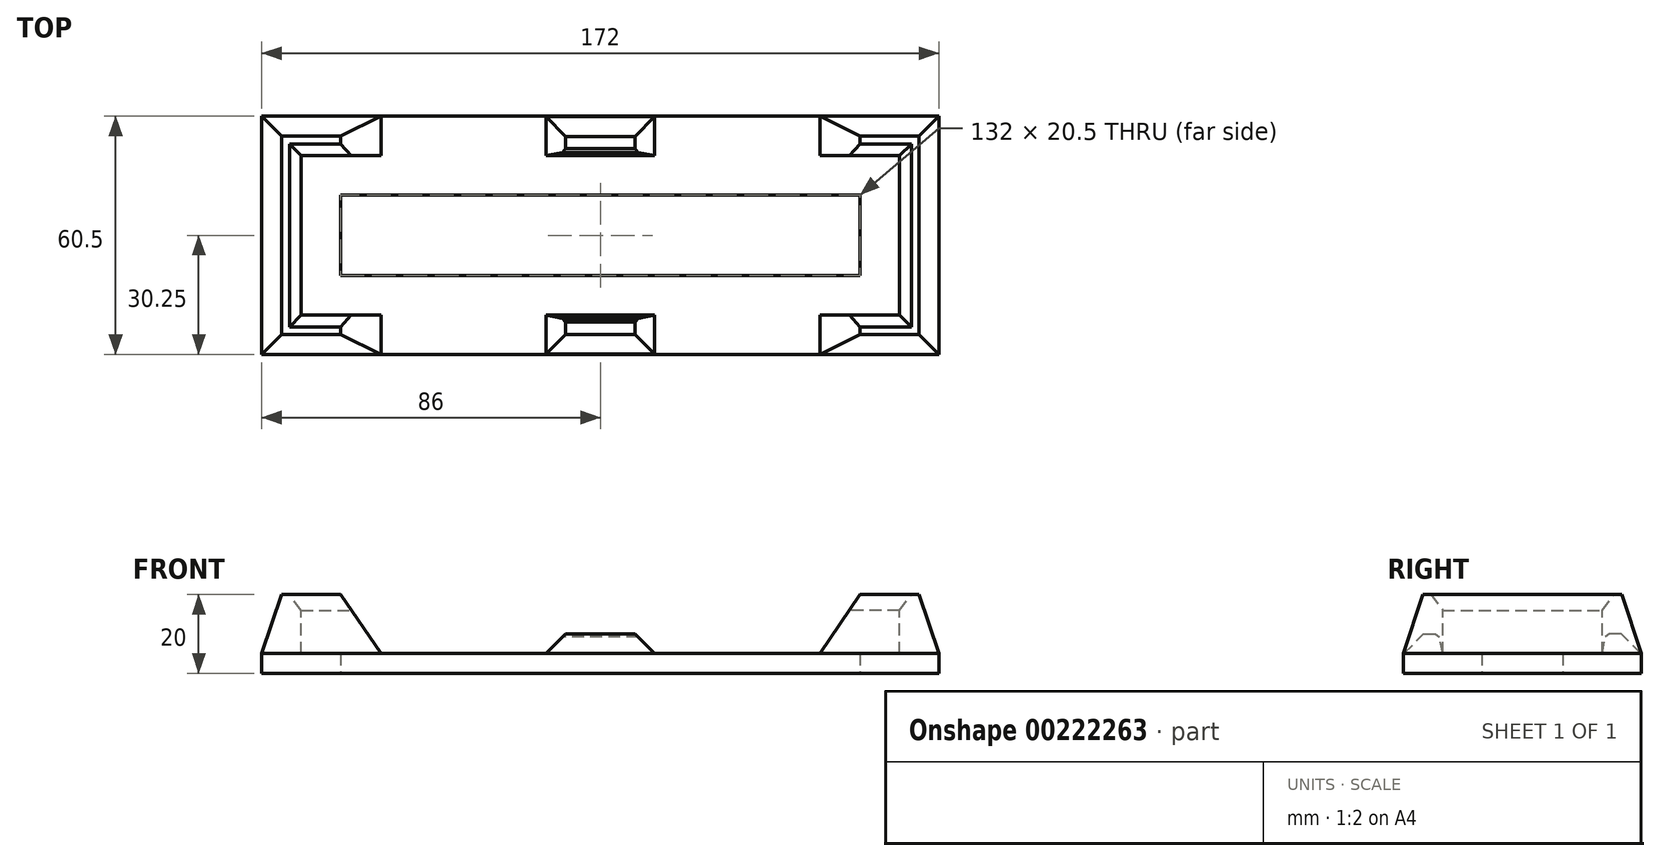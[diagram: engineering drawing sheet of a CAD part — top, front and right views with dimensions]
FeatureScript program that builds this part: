
annotation { "Feature Type Name" : "Feature", "Feature Type Description" : "" }
export const myFeature = defineFeature(function(context is Context, id is Id, definition is map)
    precondition{}
    {
        {
            var Q0;
            Q0=qCreatedBy(makeId("Top.planeOp"),FACE);
            var sketch = newSketch(context, id + "F0", { "sketchPlane" : qUnion([Q0])});
            skLineSegment(sketch, "E0.bottom", {"start": v(76, -20.25) * mm, "end": v(-76, -20.25) * mm, "construction": true});
            skLineSegment(sketch, "E0.top", {"start": v(76, 20.25) * mm, "end": v(-76, 20.25) * mm, "construction": true});
            skLineSegment(sketch, "E0.left", {"start": v(76, -20.25) * mm, "end": v(76, 20.25) * mm, "construction": true});
            skLineSegment(sketch, "E0.right", {"start": v(-76, -20.25) * mm, "end": v(-76, 20.25) * mm, "construction": true});
            skPoint(sketch, "E0.middle", {"position": v(0, 0) * mm});
            skLineSegment(sketch, "E1.bottom", {"start": v(86, -30.25) * mm, "end": v(-86, -30.25) * mm});
            skLineSegment(sketch, "E1.top", {"start": v(86, 30.25) * mm, "end": v(-86, 30.25) * mm});
            skLineSegment(sketch, "E1.left", {"start": v(86, -30.25) * mm, "end": v(86, 30.25) * mm});
            skLineSegment(sketch, "E1.right", {"start": v(-86, -30.25) * mm, "end": v(-86, 30.25) * mm});
            skSolve(sketch);
        }
        {
            var Q0;
            Q0=qCreatedBy(makeId("Top.planeOp"),FACE);
            cPlane(context, id + "F1", {"entities" : qUnion([Q0]), "cplaneType" : CPlaneType.OFFSET, "offset" : 15 * mm, "width" : 150 * mm, "height" : 150 * mm});
        }
        {
            var Q0;
            Q0=qCreatedBy(id+"F1.planeOp",FACE);
            var sketch = newSketch(context, id + "F2", { "sketchPlane" : qUnion([Q0])});
            skPoint(sketch, "E2.0", {"position": v(-86, -30.25) * mm});
            skPoint(sketch, "E3.0", {"position": v(-76, -20.25) * mm});
            skLineSegment(sketch, "E4", {"start": v(-76, 0) * mm, "end": v(-76, -20.25) * mm});
            skLineSegment(sketch, "E5", {"start": v(-76, -20.25) * mm, "end": v(-86, -30.25) * mm, "construction": true});
            skPoint(sketch, "E6", {"position": v(-81, -25.25) * mm});
            skLineSegment(sketch, "E7", {"start": v(-76, 0) * mm, "end": v(-81, 0) * mm});
            skLineSegment(sketch, "E8", {"start": v(-81, 0) * mm, "end": v(-81, -25.25) * mm});
            skLineSegment(sketch, "E9", {"start": v(-76, -20.25) * mm, "end": v(-66, -20.25) * mm});
            skLineSegment(sketch, "E10", {"start": v(-66, -20.25) * mm, "end": v(-66, -25.25) * mm});
            skLineSegment(sketch, "E11", {"start": v(-66, -25.25) * mm, "end": v(-81, -25.25) * mm});
            skSolve(sketch);
        }
        {
            var Q0;
            Q0=qCreatedBy(makeId("Top.planeOp"),FACE);
            var sketch = newSketch(context, id + "F3", { "sketchPlane" : qUnion([Q0])});
            skPoint(sketch, "E12.0", {"position": v(-86, -30.25) * mm});
            skPoint(sketch, "E13.0", {"position": v(-76, -20.25) * mm});
            skLineSegment(sketch, "E14", {"start": v(-86, -30.25) * mm, "end": v(-86, 0) * mm});
            skLineSegment(sketch, "E15", {"start": v(-86, 0) * mm, "end": v(-76, 0) * mm});
            skLineSegment(sketch, "E16", {"start": v(-76, 0) * mm, "end": v(-76, -20.25) * mm});
            skLineSegment(sketch, "E17", {"start": v(-76, -20.25) * mm, "end": v(-86, -30.25) * mm, "construction": true});
            skLineSegment(sketch, "E18.MirrorCS", {"start": v(-55.75, -20.25) * mm, "end": v(-76, -20.25) * mm});
            skLineSegment(sketch, "E19.MirrorCS", {"start": v(-86, -30.25) * mm, "end": v(-55.75, -30.25) * mm});
            skLineSegment(sketch, "E20.MirrorCS", {"start": v(-55.75, -30.25) * mm, "end": v(-55.75, -20.25) * mm});
            skLineSegment(sketch, "E21", {"start": v(0, 0) * mm, "end": v(-88.2, 0) * mm, "construction": true});
            skSolve(sketch);
        }
        {
            var Q0;
            Q0=makeQuery(id+"F0.imprint","IMPRINT",FACE,{"disambiguationData":[TD([[makeQuery(id+"F0.imprint","IMPRINT",EDGE,{"derivedFrom":sQuery(id+"F0.wireOp",EDGE,"E1.bottom")}),-1.0]])]});
            extrude(context, id + "F4", {"entities" : qUnion([Q0]), "oppositeDirection" : true, "depth" : 5 * mm});
        }
        {
            var Q1;
            Q1=makeQuery(id+"F3.imprint","IMPRINT",FACE,{"disambiguationData":[TD([[makeQuery(id+"F3.imprint","IMPRINT",EDGE,{"derivedFrom":sQuery(id+"F3.wireOp",EDGE,"E14")}),-1.0]])]});
            var Q2;
            Q2=makeQuery(id+"F2.imprint","IMPRINT",FACE,{"disambiguationData":[TD([[makeQuery(id+"F2.imprint","IMPRINT",EDGE,{"derivedFrom":sQuery(id+"F2.wireOp",EDGE,"E4")}),-1.0]])]});
            loft(context, id + "F5", {"operationType" : NewBodyOperationType.ADD, "sheetProfilesArray" : [{ "sheetProfileEntities" : qUnion([Q1]) }, { "sheetProfileEntities" : qUnion([Q2]) }]});
        }
        {
            var Q0;
            Q0=makeQuery(id+"F5.opLoft","MID_CAP_EDGE",EDGE,{"disambiguationData":[OSD([sQuery(id+"F2.wireOp",EDGE,"E4"),sQuery(id+"F2.wireOp",EDGE,"E7"),sQuery(id+"F2.wireOp",EDGE,"E9")])],"capPos":1.0});
            var Q1;
            Q1=makeQuery(id+"F5.opLoft","MID_CAP_EDGE",EDGE,{"disambiguationData":[OSD([sQuery(id+"F2.wireOp",EDGE,"E4"),sQuery(id+"F2.wireOp",EDGE,"E9"),sQuery(id+"F2.wireOp",EDGE,"E10")])],"capPos":1.0});
            chamfer(context, id + "F6", {"entities" : qUnion([Q0, Q1]), "chamferType" : ChamferType.TWO_OFFSETS, "width1" : 3 * mm, "oppositeDirection" : false, "width2" : 4 * mm, "tangentPropagation" : true});
        }
        {
            var Q0;
            Q0=makeQuery(id+"F4.opExtrude","SWEPT_BODY",BODY,{"disambiguationData":[OSD([sQuery(id+"F0.wireOp",EDGE,"E1.bottom"),sQuery(id+"F0.wireOp",EDGE,"E1.top"),sQuery(id+"F0.wireOp",EDGE,"E1.left"),sQuery(id+"F0.wireOp",EDGE,"E1.right")])]});
            var Q1;
            Q1=qCreatedBy(makeId("Right.planeOp"),FACE);
            mirror(context, id + "F7", {"operationType" : NewBodyOperationType.ADD, "entities" : qUnion([Q0]), "mirrorPlane" : qUnion([Q1])});
        }
        {
            var Q0;
            Q0=makeQuery(id+"F0.imprint","IMPRINT",FACE,{"disambiguationData":[TD([[makeQuery(id+"F0.imprint","IMPRINT",EDGE,{"derivedFrom":sQuery(id+"F0.wireOp",EDGE,"E1.bottom")}),-1.0]])]});
            var sketch = newSketch(context, id + "F8", { "sketchPlane" : qUnion([Q0])});
            skLineSegment(sketch, "E22", {"start": v(0, 45.4) * mm, "end": v(0, -36.03) * mm, "construction": true});
            skLineSegment(sketch, "E23", {"start": v(0, -20.25) * mm, "end": v(13.82, -20.25) * mm});
            skLineSegment(sketch, "E24", {"start": v(13.82, -20.25) * mm, "end": v(13.82, -30.13) * mm});
            skLineSegment(sketch, "E25", {"start": v(13.82, -30.13) * mm, "end": v(0, -30.13) * mm});
            skLineSegment(sketch, "E26.MirrorCS", {"start": v(-13.82, -30.13) * mm, "end": v(0, -30.13) * mm});
            skLineSegment(sketch, "E27.MirrorCS", {"start": v(0, -20.25) * mm, "end": v(-13.82, -20.25) * mm});
            skLineSegment(sketch, "E28.MirrorCS", {"start": v(-13.82, -20.25) * mm, "end": v(-13.82, -30.13) * mm});
            skSolve(sketch);
        }
        {
            var Q0;
            Q0 = qSketchRegion(id + "F8", true);
            extrude(context, id + "F9", {"entities" : qUnion([Q0]), "operationType" : NewBodyOperationType.ADD, "depth" : 5 * mm});
        }
        {
            var Q0;
            Q0=makeQuery(id+"F9.opExtrude","CAP_EDGE",EDGE,{"disambiguationData":[OSD([sQuery(id+"F8.wireOp",EDGE,"E24")])],"isStart":false});
            var Q1;
            Q1=makeQuery(id+"F9.opExtrude","CAP_EDGE",EDGE,{"disambiguationData":[OSD([sQuery(id+"F8.wireOp",EDGE,"E25"),sQuery(id+"F8.wireOp",EDGE,"E26.MirrorCS")])],"isStart":false});
            var Q2;
            Q2=makeQuery(id+"F9.opExtrude","CAP_EDGE",EDGE,{"disambiguationData":[OSD([sQuery(id+"F8.wireOp",EDGE,"E28.MirrorCS")])],"isStart":false});
            chamfer(context, id + "F10", {"entities" : qUnion([Q0, Q1, Q2]), "width" : 5 * mm, "tangentPropagation" : true});
        }
        {
            var Q0;
            Q0=makeQuery(id+"F9.opExtrude","CAP_EDGE",EDGE,{"disambiguationData":[OSD([sQuery(id+"F8.wireOp",EDGE,"E23"),sQuery(id+"F8.wireOp",EDGE,"E27.MirrorCS")])],"isStart":false});
            chamfer(context, id + "F11", {"entities" : qUnion([Q0]), "chamferType" : ChamferType.TWO_OFFSETS, "width1" : 5 * mm, "oppositeDirection" : false, "width2" : 1 * mm, "tangentPropagation" : true});
        }
        {
            var Q0;
            {var subQ0=sQuery(id+"F8.wireOp",EDGE,"E27.MirrorCS");var subQ1=sQuery(id+"F8.wireOp",EDGE,"E23");Q0=makeQuery(id+"F11.opChamfer","BLEND_EDGE",EDGE,{"blendedFrom":[makeQuery(id+"F9.opExtrude","CAP_EDGE",EDGE,{"disambiguationData":[OSD([subQ1,subQ0])],"isStart":false}),makeQuery(id+"F9.opExtrude","CAP_FACE",FACE,{"disambiguationData":[OSD([subQ1,sQuery(id+"F8.wireOp",EDGE,"E24"),sQuery(id+"F8.wireOp",EDGE,"E25"),subQ0,sQuery(id+"F8.wireOp",EDGE,"E28.MirrorCS"),sQuery(id+"F8.wireOp",EDGE,"E26.MirrorCS")])],"isStart":false})],"blendedInto":[makeQuery(id+"F9.opExtrude","CAP_FACE",FACE,{"disambiguationData":[OSD([subQ1,sQuery(id+"F8.wireOp",EDGE,"E24"),sQuery(id+"F8.wireOp",EDGE,"E25"),subQ0,sQuery(id+"F8.wireOp",EDGE,"E28.MirrorCS"),sQuery(id+"F8.wireOp",EDGE,"E26.MirrorCS")])],"isStart":false})]});}
            chamfer(context, id + "F12", {"entities" : qUnion([Q0]), "width" : 1 * mm, "tangentPropagation" : true});
        }
        {
            var Q0;
            Q0=makeQuery(id+"F4.opExtrude","SWEPT_BODY",BODY,{"disambiguationData":[OSD([sQuery(id+"F0.wireOp",EDGE,"E1.bottom"),sQuery(id+"F0.wireOp",EDGE,"E1.top"),sQuery(id+"F0.wireOp",EDGE,"E1.left"),sQuery(id+"F0.wireOp",EDGE,"E1.right")])]});
            var Q1;
            Q1=qCreatedBy(makeId("Front.planeOp"),FACE);
            mirror(context, id + "F13", {"operationType" : NewBodyOperationType.ADD, "entities" : qUnion([Q0]), "mirrorPlane" : qUnion([Q1])});
        }
        {
            var Q0;
            Q0=qCreatedBy(makeId("Top.planeOp"),FACE);
            var sketch = newSketch(context, id + "F14", { "sketchPlane" : qUnion([Q0])});
            skLineSegment(sketch, "E29.bottom", {"start": v(66, -10.25) * mm, "end": v(-66, -10.25) * mm});
            skLineSegment(sketch, "E29.top", {"start": v(66, 10.25) * mm, "end": v(-66, 10.25) * mm});
            skLineSegment(sketch, "E29.left", {"start": v(66, -10.25) * mm, "end": v(66, 10.25) * mm});
            skLineSegment(sketch, "E29.right", {"start": v(-66, -10.25) * mm, "end": v(-66, 10.25) * mm});
            skPoint(sketch, "E29.middle", {"position": v(0, 0) * mm});
            skLineSegment(sketch, "E30.0", {"start": v(-76, -20.25) * mm, "end": v(-76, 20.25) * mm, "construction": true});
            skLineSegment(sketch, "E31.0", {"start": v(76, 20.25) * mm, "end": v(-76, 20.25) * mm, "construction": true});
            skSolve(sketch);
        }
        {
            var Q0;
            Q0=qSketchRegion(id+"F14",true);
            extrude(context, id + "F15", {"entities" : qUnion([Q0]), "operationType" : NewBodyOperationType.REMOVE, "endBound" : BoundingType.SYMMETRIC, "depth" : 25 * mm});
        }
    });
